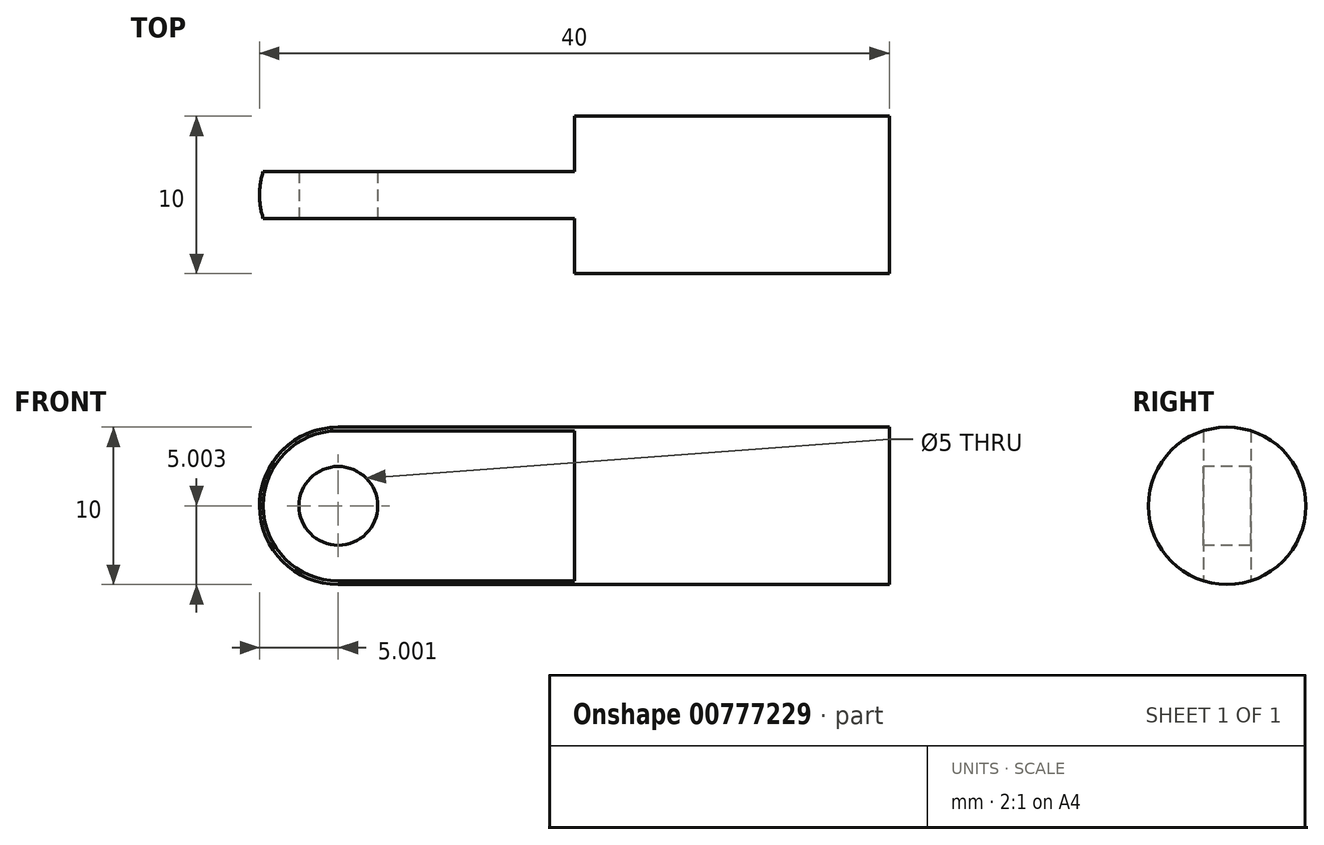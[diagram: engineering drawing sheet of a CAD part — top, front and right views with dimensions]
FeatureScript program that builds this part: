
annotation { "Feature Type Name" : "Feature", "Feature Type Description" : "" }
export const myFeature = defineFeature(function(context is Context, id is Id, definition is map)
    precondition{}
    {
        {
            var Q0;
            Q0=qCreatedBy(makeId("Front.planeOp"),FACE);
            var sketch = newSketch(context, id + "F0", { "sketchPlane" : qUnion([Q0])});
            skLineSegment(sketch, "E0.bottom", {"start": v(-33.69, 15.45) * mm, "end": v(-13.69, 15.45) * mm});
            skLineSegment(sketch, "E0.top", {"start": v(-33.69, 10.45) * mm, "end": v(-13.69, 10.45) * mm});
            skLineSegment(sketch, "E0.left", {"start": v(-33.69, 15.45) * mm, "end": v(-33.69, 10.45) * mm});
            skLineSegment(sketch, "E0.right", {"start": v(-13.69, 15.45) * mm, "end": v(-13.69, 10.45) * mm});
            skSolve(sketch);
        }
        {
            var Q0;
            Q0=makeQuery(id+"F0.imprint","IMPRINT",FACE,{"disambiguationData":[TD([[makeQuery(id+"F0.imprint","IMPRINT",EDGE,{"derivedFrom":sQuery(id+"F0.wireOp",EDGE,"E0.bottom")}),-1.0]])]});
            var Q1;
            Q1=sQuery(id+"F0.wireOp",EDGE,"E0.top");
            revolve(context, id + "F1", {"surfaceOperationType" : NewSurfaceOperationType.NEW, "entities" : qUnion([Q0]), "axis" : qUnion([Q1]), "revolveType" : RevolveType.FULL});
        }
        {
            var Q0;
            Q0=makeQuery(id+"F1.opRevolve","SWEPT_FACE",FACE,{"disambiguationData":[OSD([sQuery(id+"F0.wireOp",EDGE,"E0.left")])]});
            var sketch = newSketch(context, id + "F2", { "sketchPlane" : qUnion([Q0])});
            skLineSegment(sketch, "E1.left", {"start": v(-1.5, 15.22) * mm, "end": v(-1.5, 5.68) * mm});
            skLineSegment(sketch, "E1.right", {"start": v(1.5, 15.22) * mm, "end": v(1.5, 5.68) * mm});
            skPoint(sketch, "E1.middle", {"position": v(0, 10.45) * mm});
            skSolve(sketch);
        }
        {
            var Q0;
            Q0 = qSketchRegion(id + "F2", true);
            var Q1;
            {var subQ0=sQuery(id+"F2.wireOp",EDGE,"E1.left");Q1=makeQuery(id+"F2.imprint","IMPRINT",FACE,{"disambiguationData":[TD([[makeQuery(id+"F2.imprint","IMPRINT",EDGE,{"derivedFrom":subQ0}),1.0]])]});}
            extrude(context, id + "F3", {"entities" : qUnion([Q0, Q1]), "operationType" : NewBodyOperationType.ADD, "depth" : 20 * mm, "offsetDistance" : 25 * mm});
        }
        {
            var Q0;
            {var subQ0=sQuery(id+"F0.wireOp",EDGE,"E0.left");var subQ1=sQuery(id+"F0.wireOp",EDGE,"E0.bottom");var subQ2=makeQuery(id+"F1.opRevolve","SWEPT_EDGE",EDGE,{"disambiguationData":[OSD([subQ1,subQ0])]});Q0=makeQuery(id+"F3.opExtrude","CAP_EDGE",EDGE,{"disambiguationData":[OSD([subQ1,subQ0]),TDD([makeQuery(id+"F2.imprint","IMPRINT",EDGE,{"disambiguationData":[TD([[makeQuery(id+"F2.imprint","INTERSECT",VERTEX,{"disambiguationData":[OD(0.0)],"derivedFrom":[subQ2,sQuery(id+"F2.wireOp",EDGE,"E1.left")]}),1.0]])],"derivedFrom":subQ2})])],"isStart":false});}
            fillet(context, id + "F4", {"entities" : qUnion([Q0]), "radius" : 5 * mm, "tangentPropagation" : true, "allowEdgeOverflow" : false});
        }
        {
            var Q0;
            Q0=makeQuery(id+"F3.opExtrude","SWEPT_FACE",FACE,{"disambiguationData":[OSD([sQuery(id+"F2.wireOp",EDGE,"E1.right")])]});
            var sketch = newSketch(context, id + "F5", { "sketchPlane" : qUnion([Q0])});
            skLineSegment(sketch, "E2", {"start": v(-53.46, 10.45) * mm, "end": v(-48.69, 10.45) * mm, "construction": true});
            skCircle(sketch, "E3", {"center": v(-48.69, 10.45) * mm, "radius": 2.5 * mm});
            skSolve(sketch);
        }
        {
            var Q0;
            Q0=makeQuery(id+"F5.imprint","IMPRINT",FACE,{"disambiguationData":[TD([[makeQuery(id+"F5.imprint","IMPRINT",EDGE,{"derivedFrom":sQuery(id+"F5.wireOp",EDGE,"E3")}),1.0]])]});
            extrude(context, id + "F6", {"entities" : qUnion([Q0]), "operationType" : NewBodyOperationType.REMOVE, "oppositeDirection" : true, "depth" : 3 * mm, "offsetDistance" : 25 * mm});
        }
    });
